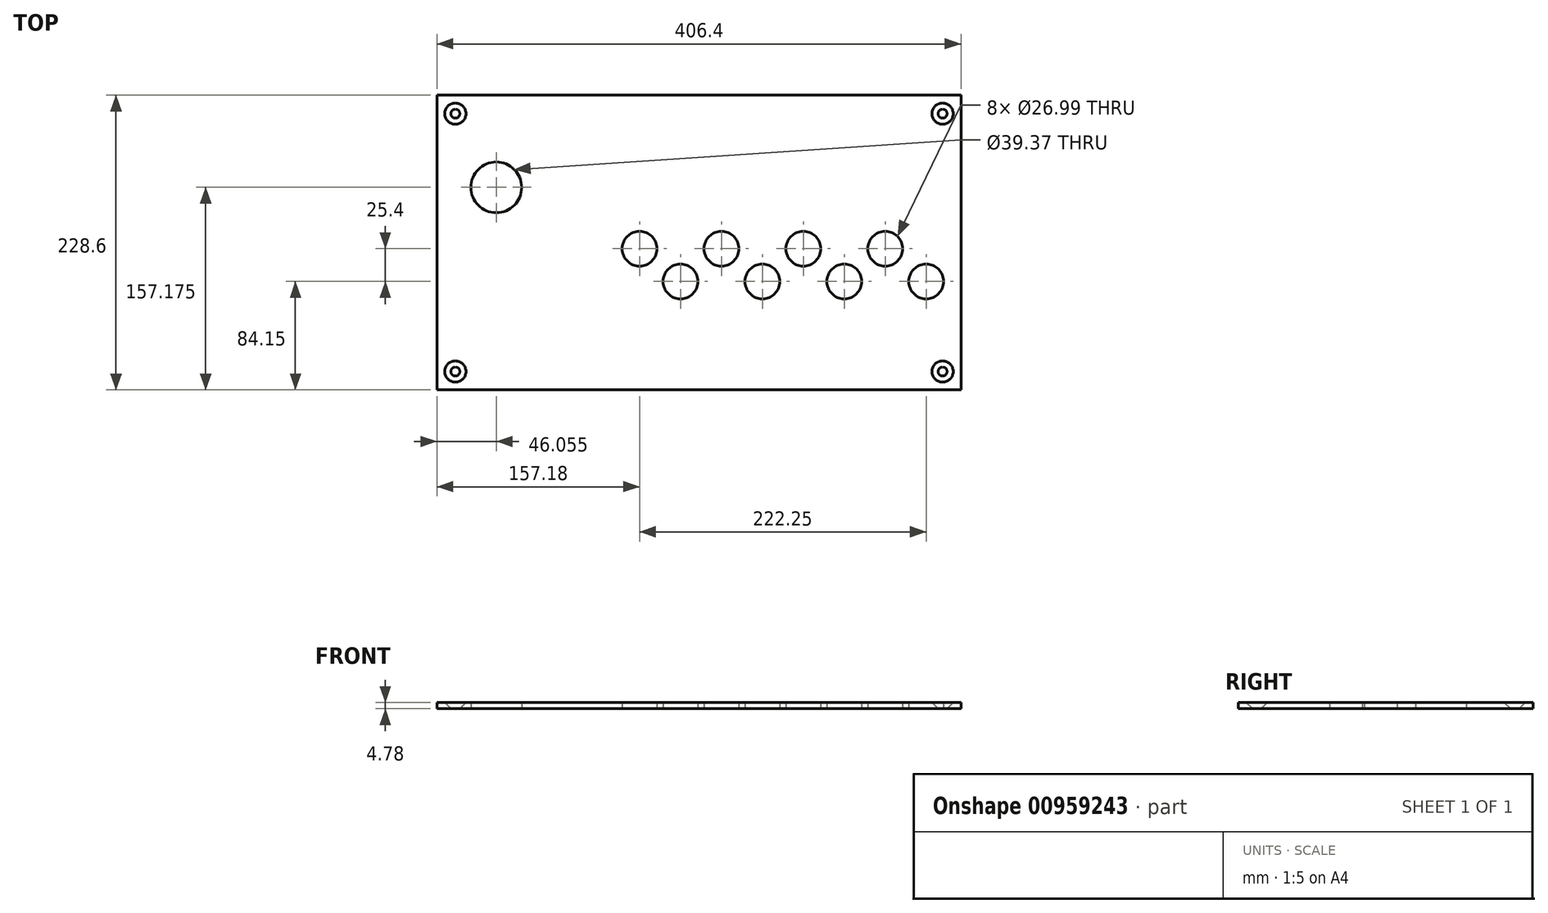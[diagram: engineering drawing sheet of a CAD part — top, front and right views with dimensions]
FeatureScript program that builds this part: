
annotation { "Feature Type Name" : "Feature", "Feature Type Description" : "" }
export const myFeature = defineFeature(function(context is Context, id is Id, definition is map)
    precondition{}
    {
        {
            var Q0;
            Q0=qCreatedBy(makeId("Top.planeOp"),FACE);
            var sketch = newSketch(context, id + "F0", { "sketchPlane" : qUnion([Q0])});
            skLineSegment(sketch, "E0.bottom", {"start": v(-224.8, 114.3) * mm, "end": v(172.09, 114.3) * mm});
            skLineSegment(sketch, "E0.top", {"start": v(-224.8, -104.78) * mm, "end": v(172.09, -104.78) * mm});
            skLineSegment(sketch, "E0.left", {"start": v(-224.8, 114.3) * mm, "end": v(-224.8, -104.78) * mm});
            skLineSegment(sketch, "E0.right", {"start": v(172.09, 114.3) * mm, "end": v(172.09, -104.78) * mm});
            skCircle(sketch, "E1", {"center": v(-72.4, 0) * mm, "radius": 13.5 * mm});
            skCircle(sketch, "E2", {"center": v(-40.64, -25.4) * mm, "radius": 13.5 * mm});
            skCircle(sketch, "E3", {"center": v(-8.89, 0) * mm, "radius": 13.5 * mm});
            skCircle(sketch, "E4", {"center": v(22.86, -25.4) * mm, "radius": 13.5 * mm});
            skCircle(sketch, "E5", {"center": v(-183.52, 47.62) * mm, "radius": 19.69 * mm});
            skCircle(sketch, "E6", {"center": v(-215.27, 104.77) * mm, "radius": 3.18 * mm});
            skCircle(sketch, "E7", {"center": v(-215.27, -95.25) * mm, "radius": 3.18 * mm});
            skCircle(sketch, "E8", {"center": v(162.56, -95.25) * mm, "radius": 3.18 * mm});
            skCircle(sketch, "E9", {"center": v(162.56, 104.77) * mm, "radius": 3.18 * mm});
            skLineSegment(sketch, "E10.bottom", {"start": v(-229.57, 119.05) * mm, "end": v(176.83, 119.05) * mm});
            skLineSegment(sketch, "E10.top", {"start": v(-229.57, -109.55) * mm, "end": v(176.83, -109.55) * mm});
            skLineSegment(sketch, "E10.left", {"start": v(-229.57, 119.05) * mm, "end": v(-229.57, -109.55) * mm});
            skLineSegment(sketch, "E10.right", {"start": v(176.83, 119.05) * mm, "end": v(176.83, -109.55) * mm});
            skCircle(sketch, "E11", {"center": v(54.61, 0) * mm, "radius": 13.5 * mm});
            skCircle(sketch, "E12", {"center": v(86.36, -25.4) * mm, "radius": 13.5 * mm});
            skCircle(sketch, "E13", {"center": v(118.11, 0) * mm, "radius": 13.5 * mm});
            skCircle(sketch, "E14", {"center": v(149.86, -25.4) * mm, "radius": 13.5 * mm});
            skSolve(sketch);
        }
        {
            var Q0;
            Q0=makeQuery(id+"F0.imprint","IMPRINT",FACE,{"disambiguationData":[TD([[makeQuery(id+"F0.imprint","IMPRINT",EDGE,{"derivedFrom":sQuery(id+"F0.wireOp",EDGE,"E0.bottom")}),-1.0]])]});
            var Q1;
            Q1=makeQuery(id+"F0.imprint","IMPRINT",FACE,{"disambiguationData":[TD([[makeQuery(id+"F0.imprint","IMPRINT",EDGE,{"derivedFrom":sQuery(id+"F0.wireOp",EDGE,"E0.bottom")}),1.0]])]});
            extrude(context, id + "F1", {"entities" : qUnion([Q0, Q1]), "depth" : 4.78 * mm, "offsetDistance" : 25.4 * mm});
        }
        {
            var Q0;
            Q0=makeQuery(id+"F1.opExtrude","CAP_EDGE",EDGE,{"disambiguationData":[OSD([sQuery(id+"F0.wireOp",EDGE,"E7")])],"isStart":false});
            var Q1;
            Q1=makeQuery(id+"F1.opExtrude","CAP_EDGE",EDGE,{"disambiguationData":[OSD([sQuery(id+"F0.wireOp",EDGE,"E6")])],"isStart":false});
            var Q2;
            Q2=makeQuery(id+"F1.opExtrude","CAP_EDGE",EDGE,{"disambiguationData":[OSD([sQuery(id+"F0.wireOp",EDGE,"E9")])],"isStart":false});
            var Q3;
            Q3=makeQuery(id+"F1.opExtrude","CAP_EDGE",EDGE,{"disambiguationData":[OSD([sQuery(id+"F0.wireOp",EDGE,"E8")])],"isStart":false});
            chamfer(context, id + "F2", {"entities" : qUnion([Q0, Q1, Q2, Q3]), "width" : 5.08 * mm, "tangentPropagation" : true});
        }
    });
